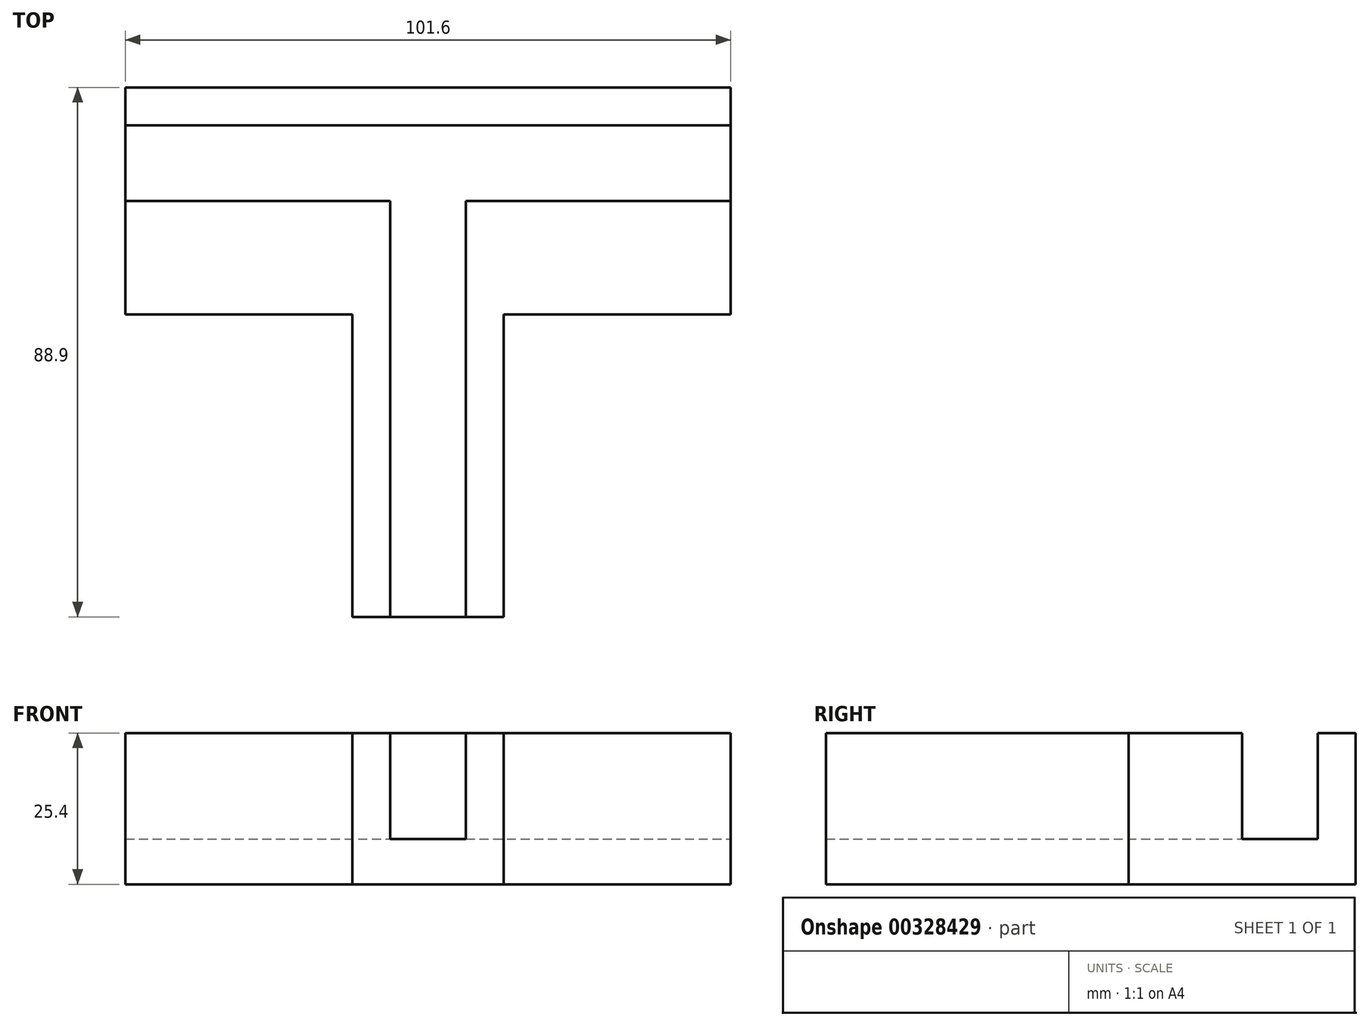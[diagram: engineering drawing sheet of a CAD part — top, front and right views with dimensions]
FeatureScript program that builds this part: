
annotation { "Feature Type Name" : "Feature", "Feature Type Description" : "" }
export const myFeature = defineFeature(function(context is Context, id is Id, definition is map)
    precondition{}
    {
        {
            var Q0;
            Q0=qCreatedBy(makeId("Top.planeOp"),FACE);
            var sketch = newSketch(context, id + "F0", { "sketchPlane" : qUnion([Q0])});
            skLineSegment(sketch, "E0.bottom", {"start": v(0, 0) * mm, "end": v(25.4, 0) * mm});
            skLineSegment(sketch, "E0.top", {"start": v(0, 50.8) * mm, "end": v(25.4, 50.8) * mm});
            skLineSegment(sketch, "E0.left", {"start": v(0, 0) * mm, "end": v(0, 50.8) * mm});
            skLineSegment(sketch, "E0.right", {"start": v(25.4, 0) * mm, "end": v(25.4, 50.8) * mm});
            skLineSegment(sketch, "E1.bottom", {"start": v(25.4, 50.8) * mm, "end": v(63.5, 50.8) * mm});
            skLineSegment(sketch, "E1.top", {"start": v(25.4, 88.9) * mm, "end": v(63.5, 88.9) * mm});
            skLineSegment(sketch, "E1.left", {"start": v(25.4, 50.8) * mm, "end": v(25.4, 88.9) * mm});
            skLineSegment(sketch, "E1.right", {"start": v(63.5, 50.8) * mm, "end": v(63.5, 88.9) * mm});
            skLineSegment(sketch, "E2.bottom", {"start": v(0, 50.8) * mm, "end": v(-38.1, 50.8) * mm});
            skLineSegment(sketch, "E2.top", {"start": v(0, 88.9) * mm, "end": v(-38.1, 88.9) * mm});
            skLineSegment(sketch, "E2.left", {"start": v(0, 50.8) * mm, "end": v(0, 88.9) * mm});
            skLineSegment(sketch, "E2.right", {"start": v(-38.1, 50.8) * mm, "end": v(-38.1, 88.9) * mm});
            skLineSegment(sketch, "E3.bottom", {"start": v(0, 88.9) * mm, "end": v(25.4, 88.9) * mm});
            skLineSegment(sketch, "E3.left", {"start": v(0, 88.9) * mm, "end": v(0, 50.8) * mm});
            skLineSegment(sketch, "E3.right", {"start": v(25.4, 88.9) * mm, "end": v(25.4, 50.8) * mm});
            skSolve(sketch);
        }
        {
            var Q0;
            Q0=makeQuery(id+"F0.imprint","IMPRINT",FACE,{"disambiguationData":[TD([[makeQuery(id+"F0.imprint","IMPRINT",EDGE,{"derivedFrom":sQuery(id+"F0.wireOp",EDGE,"E0.bottom")}),1.0]])]});
            var Q1;
            Q1=makeQuery(id+"F0.imprint","IMPRINT",FACE,{"disambiguationData":[TD([[makeQuery(id+"F0.imprint","IMPRINT",EDGE,{"derivedFrom":sQuery(id+"F0.wireOp",EDGE,"E1.bottom")}),1.0]])]});
            var Q2;
            Q2=makeQuery(id+"F0.imprint","IMPRINT",FACE,{"disambiguationData":[TD([[makeQuery(id+"F0.imprint","IMPRINT",EDGE,{"derivedFrom":sQuery(id+"F0.wireOp",EDGE,"E3.bottom")}),-1.0]])]});
            var Q3;
            Q3=makeQuery(id+"F0.imprint","IMPRINT",FACE,{"disambiguationData":[TD([[makeQuery(id+"F0.imprint","IMPRINT",EDGE,{"derivedFrom":sQuery(id+"F0.wireOp",EDGE,"E2.bottom")}),-1.0]])]});
            extrude(context, id + "F1", {"entities" : qUnion([Q0, Q1, Q2, Q3]), "depth" : 25.4 * mm});
        }
        {
            var Q0;
            Q0=makeQuery(id+"F1.opExtrude","CAP_FACE",FACE,{"disambiguationData":[OSD([sQuery(id+"F0.wireOp",EDGE,"E0.bottom"),sQuery(id+"F0.wireOp",EDGE,"E0.left"),sQuery(id+"F0.wireOp",EDGE,"E0.right"),sQuery(id+"F0.wireOp",EDGE,"E1.bottom"),sQuery(id+"F0.wireOp",EDGE,"E1.top"),sQuery(id+"F0.wireOp",EDGE,"E1.right"),sQuery(id+"F0.wireOp",EDGE,"E2.bottom"),sQuery(id+"F0.wireOp",EDGE,"E2.top"),sQuery(id+"F0.wireOp",EDGE,"E2.right"),sQuery(id+"F0.wireOp",EDGE,"E3.bottom")])],"isStart":false});
            var sketch = newSketch(context, id + "F2", { "sketchPlane" : qUnion([Q0])});
            skLineSegment(sketch, "E4.bottom", {"start": v(6.35, 0) * mm, "end": v(19.05, 0) * mm});
            skLineSegment(sketch, "E4.top", {"start": v(6.35, 50.8) * mm, "end": v(19.05, 50.8) * mm});
            skLineSegment(sketch, "E4.left", {"start": v(6.35, 0) * mm, "end": v(6.35, 50.8) * mm});
            skLineSegment(sketch, "E4.right", {"start": v(19.05, 0) * mm, "end": v(19.05, 50.8) * mm});
            skLineSegment(sketch, "E5.bottom", {"start": v(-38.1, 69.85) * mm, "end": v(63.5, 69.85) * mm});
            skLineSegment(sketch, "E5.top", {"start": v(-38.1, 82.55) * mm, "end": v(63.5, 82.55) * mm});
            skLineSegment(sketch, "E5.left", {"start": v(-38.1, 69.85) * mm, "end": v(-38.1, 82.55) * mm});
            skLineSegment(sketch, "E5.right", {"start": v(63.5, 69.85) * mm, "end": v(63.5, 82.55) * mm});
            skLineSegment(sketch, "E6.top", {"start": v(6.35, 69.85) * mm, "end": v(19.05, 69.85) * mm});
            skLineSegment(sketch, "E6.left", {"start": v(6.35, 50.8) * mm, "end": v(6.35, 69.85) * mm});
            skLineSegment(sketch, "E6.right", {"start": v(19.05, 50.8) * mm, "end": v(19.05, 69.85) * mm});
            skSolve(sketch);
        }
        {
            var Q0;
            Q0=makeQuery(id+"F2.imprint","IMPRINT",FACE,{"disambiguationData":[TD([[makeQuery(id+"F2.imprint","IMPRINT",EDGE,{"derivedFrom":sQuery(id+"F2.wireOp",EDGE,"E5.top")}),-1.0]])]});
            var Q1;
            Q1=makeQuery(id+"F2.imprint","IMPRINT",FACE,{"disambiguationData":[TD([[makeQuery(id+"F2.imprint","IMPRINT",EDGE,{"derivedFrom":sQuery(id+"F2.wireOp",EDGE,"E4.top")}),1.0]])]});
            var Q2;
            Q2=makeQuery(id+"F2.imprint","IMPRINT",FACE,{"disambiguationData":[TD([[makeQuery(id+"F2.imprint","IMPRINT",EDGE,{"derivedFrom":sQuery(id+"F2.wireOp",EDGE,"E4.bottom")}),1.0]])]});
            extrude(context, id + "F3", {"entities" : qUnion([Q0, Q1, Q2]), "operationType" : NewBodyOperationType.REMOVE, "oppositeDirection" : true, "depth" : 17.78 * mm});
        }
    });
